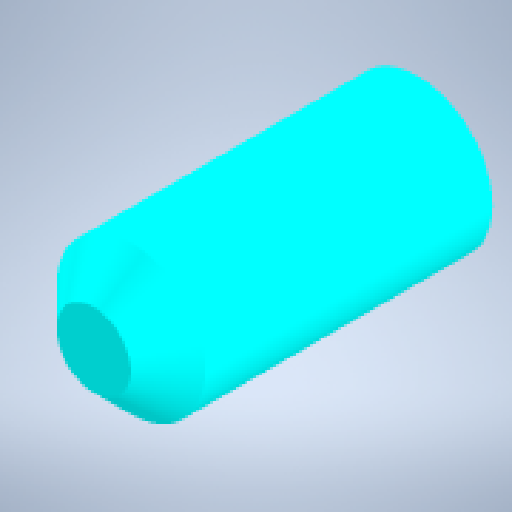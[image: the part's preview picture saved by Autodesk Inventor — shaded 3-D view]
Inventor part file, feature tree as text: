
AUTODESK INVENTOR PART (.ipt)
format: ipt  version: 2023.1 (Build 271208000, 208)  size: 204,288 bytes
history: native  units: mm
features: other x2, sketch x1, plane x1, extrude x1, chamfer x1, reference x1
ambient origin geometry x8: Origin, YZ Plane, XZ Plane, XY Plane, X Axis, Y Axis, Z Axis, Center Point
bodies: Solid1 (feature_tree)
feature tree (7):
  sketch  "Sketch1"  dims[d0=43.75mm d1=0.0mm d2=5.0mm d3=2.0mm d4=45.0deg]
  plane  "Work Plane3"
  extrude  "Extrusion1"  Depth=43.75mm TaperAngle=45.0deg
  chamfer  "Chamfer1"  [1 undecoded]
  reference  "Reference1"
  other  "Sample Z Axis Fit Test.iam"
  other  "Objective Mount:1"
note: 1 required parameter value undecoded (feature->parameter linkage not recoverable at this tier; creation-order binding heuristic only, values carry confidence <= 0.55)
